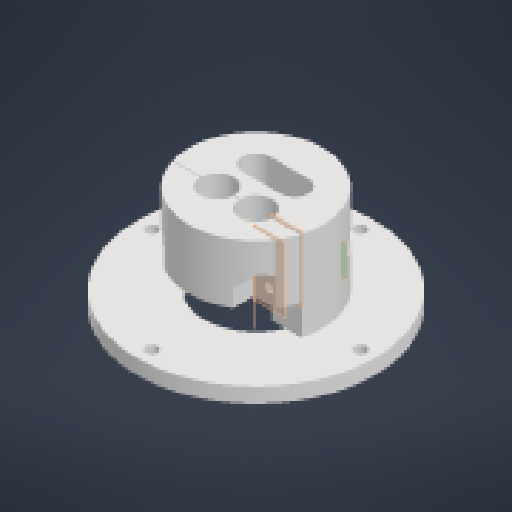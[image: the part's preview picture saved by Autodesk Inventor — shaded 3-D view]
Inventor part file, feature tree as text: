
AUTODESK INVENTOR PART (.ipt)
format: ipt  version: 2023.2 (Build 272271000, 271)  size: 303,616 bytes
history: native  units: mm
features: sketch x8, extrude x8, plane x3, other x1, pattern_circular x1, mirror x1, split x1
ambient origin geometry x8: Origin, YZ Plane, XZ Plane, XY Plane, X Axis, Y Axis, Z Axis, Center Point
bodies: Solid1 (feature_tree), Solid6 (feature_tree), Solid7 (feature_tree)
feature tree (23):
  sketch  "Sketch1"  dims[d0=13.0mm d1=13.0mm]
  extrude  "Extrusion1"  Depth=13.0mm
  extrude  "Extrusion2"  Depth=10.9mm
  extrude  "Extrusion3"  Depth=45.0mm
  extrude  "Extrusion4"  Depth=0.2mm
  other  "Work Axis1"
  pattern_circular  "Circular Pattern1"  Count=2  [1 undecoded]
  extrude  "Extrusion5"  Depth=10.0mm
  plane  "Work Plane1"
  extrude  "Extrusion6"  Depth=5.0mm TaperAngle=0.0deg
  mirror  "Mirror1"
  plane  "Work Plane2"
  plane  "Work Plane3"
  extrude  "Extrusion9"  Depth=5.0mm TaperAngle=360.0deg
  extrude  "Extrusion10"  Depth=10.0mm TaperAngle=0.0deg
  split  "Split3"
  sketch  "Sketch2"  dims[d2=10.9mm d3=10.9mm]
  sketch  "Sketch3"  dims[d4=9.0mm d5=45.0mm]
  sketch  "Sketch4"  dims[d6=60.0mm d7=0.2mm d8=20.0mm d9=0.0mm]
  sketch  "Sketch5"  dims[d10=10.0mm d11=0.0mm d12=35.0mm]
  sketch  "Sketch11"  dims[d13=80.0mm d14=5.0mm d15=0.0mm]
  sketch  "Sketch12"  dims[d17=5.0mm d18=0.0mm d19=40.0mm d20=360.0deg]
  sketch  "Sketch13"  dims[d22=3.0mm d23=30.0mm d24=15.0mm d25=0.0mm d26=0.0mm d27=15.0mm d28=5.5mm d29=30.0mm d30=0.0mm d31=0.0mm d34=6.0mm d40=10.0mm d41=0.0mm d42=10.0mm d43=0.0mm d44=4.0mm d37=0.5mm d38=0.872665mm d39=0.5mm]
note: 1 required parameter value undecoded (feature->parameter linkage not recoverable at this tier; creation-order binding heuristic only, values carry confidence <= 0.55)
